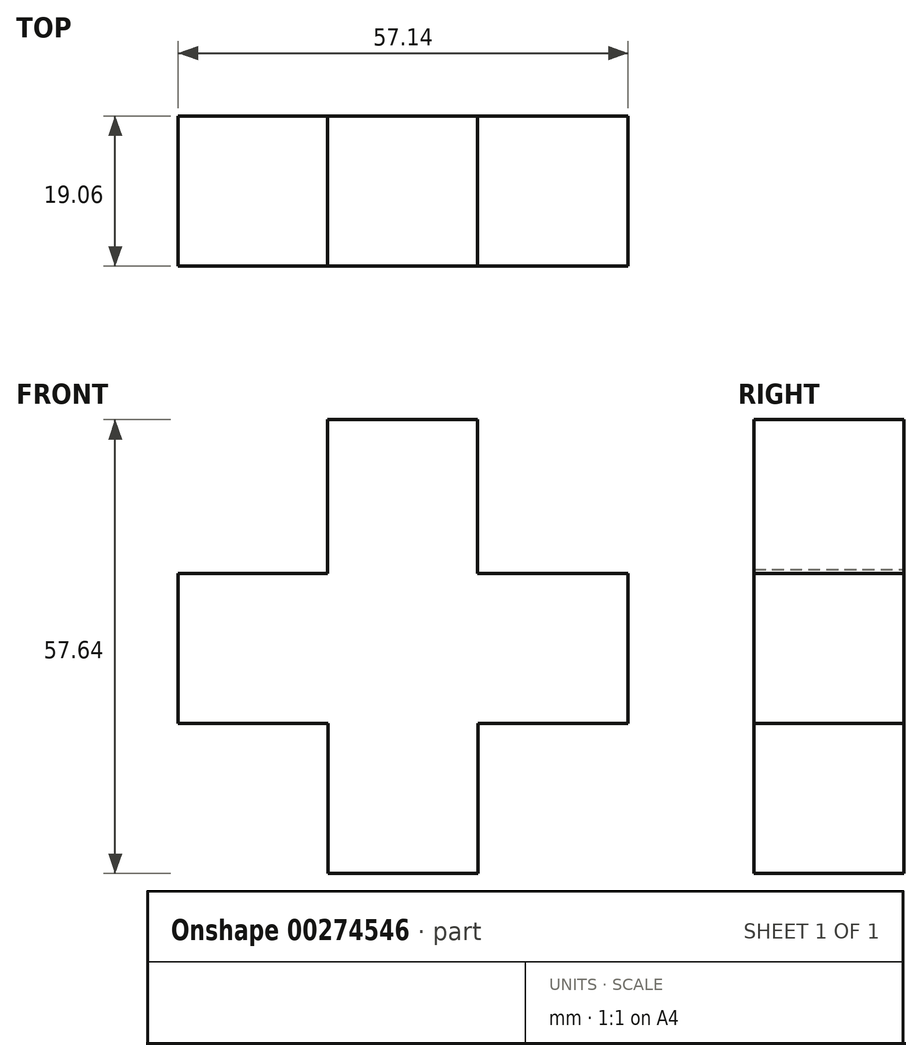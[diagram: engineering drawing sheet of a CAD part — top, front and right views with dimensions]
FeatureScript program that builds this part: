
annotation { "Feature Type Name" : "Feature", "Feature Type Description" : "" }
export const myFeature = defineFeature(function(context is Context, id is Id, definition is map)
    precondition{}
    {
        {
            var Q0;
            Q0=qCreatedBy(makeId("Front.planeOp"),FACE);
            var sketch = newSketch(context, id + "F0", { "sketchPlane" : qUnion([Q0])});
            skLineSegment(sketch, "E0.bottom", {"start": v(-9.53, 9.53) * mm, "end": v(9.53, 9.53) * mm});
            skLineSegment(sketch, "E0.top", {"start": v(-9.53, -9.53) * mm, "end": v(9.53, -9.53) * mm});
            skLineSegment(sketch, "E0.left", {"start": v(-9.53, 9.53) * mm, "end": v(-9.53, -9.53) * mm});
            skLineSegment(sketch, "E0.right", {"start": v(9.53, 9.53) * mm, "end": v(9.53, -9.53) * mm});
            skPoint(sketch, "E0.middle", {"position": v(0, 0) * mm});
            skLineSegment(sketch, "E1.bottom", {"start": v(-9.52, 28.58) * mm, "end": v(9.53, 28.58) * mm});
            skLineSegment(sketch, "E1.left", {"start": v(-9.53, 28.58) * mm, "end": v(-9.53, 9.85) * mm});
            skLineSegment(sketch, "E1.right", {"start": v(9.53, 28.58) * mm, "end": v(9.53, 9.85) * mm});
            skPoint(sketch, "E1.middle", {"position": v(0, 19.21) * mm});
            skLineSegment(sketch, "E2.bottom", {"start": v(9.53, 28.58) * mm, "end": v(28.57, 28.58) * mm});
            skLineSegment(sketch, "E2.top", {"start": v(9.53, 9.53) * mm, "end": v(28.57, 9.53) * mm});
            skLineSegment(sketch, "E2.left", {"start": v(9.53, 28.58) * mm, "end": v(9.53, 9.53) * mm});
            skLineSegment(sketch, "E2.right", {"start": v(28.57, 28.58) * mm, "end": v(28.57, 9.53) * mm});
            skPoint(sketch, "E2.middle", {"position": v(19.05, 19.05) * mm});
            skLineSegment(sketch, "E3", {"start": v(-9.52, 9.85) * mm, "end": v(28.57, 9.53) * mm});
            skLineSegment(sketch, "E4.bottom", {"start": v(-9.52, 28.58) * mm, "end": v(-28.57, 28.58) * mm});
            skLineSegment(sketch, "E4.top", {"start": v(-9.52, 9.53) * mm, "end": v(-28.57, 9.53) * mm});
            skLineSegment(sketch, "E4.left", {"start": v(-9.52, 28.58) * mm, "end": v(-9.52, 9.53) * mm});
            skLineSegment(sketch, "E4.right", {"start": v(-28.57, 28.58) * mm, "end": v(-28.57, 9.53) * mm});
            skPoint(sketch, "E4.middle", {"position": v(-19.05, 19.05) * mm});
            skLineSegment(sketch, "E5.bottom", {"start": v(-9.6, 48.11) * mm, "end": v(9.46, 48.11) * mm});
            skLineSegment(sketch, "E5.top", {"start": v(-9.6, 29.06) * mm, "end": v(9.46, 29.06) * mm});
            skLineSegment(sketch, "E5.left", {"start": v(-9.6, 48.11) * mm, "end": v(-9.6, 29.06) * mm});
            skLineSegment(sketch, "E5.right", {"start": v(9.46, 48.11) * mm, "end": v(9.46, 29.06) * mm});
            skPoint(sketch, "E5.middle", {"position": v(-0.07, 38.59) * mm});
            skLineSegment(sketch, "E6", {"start": v(-9.6, 48.11) * mm, "end": v(-9.53, -9.52) * mm});
            skLineSegment(sketch, "E7", {"start": v(9.53, -9.52) * mm, "end": v(9.46, 48.11) * mm});
            skLineSegment(sketch, "E8", {"start": v(-28.57, 28.58) * mm, "end": v(28.57, 28.58) * mm});
            skLineSegment(sketch, "E9", {"start": v(28.57, 9.53) * mm, "end": v(-28.57, 9.53) * mm});
            skSolve(sketch);
        }
        {
            var Q0;
            Q0 = qSketchRegion(id + "F0", true);
            extrude(context, id + "F1", {"entities" : qUnion([Q0]), "endBound" : BoundingType.SYMMETRIC, "depth" : 19.05 * mm});
        }
    });
